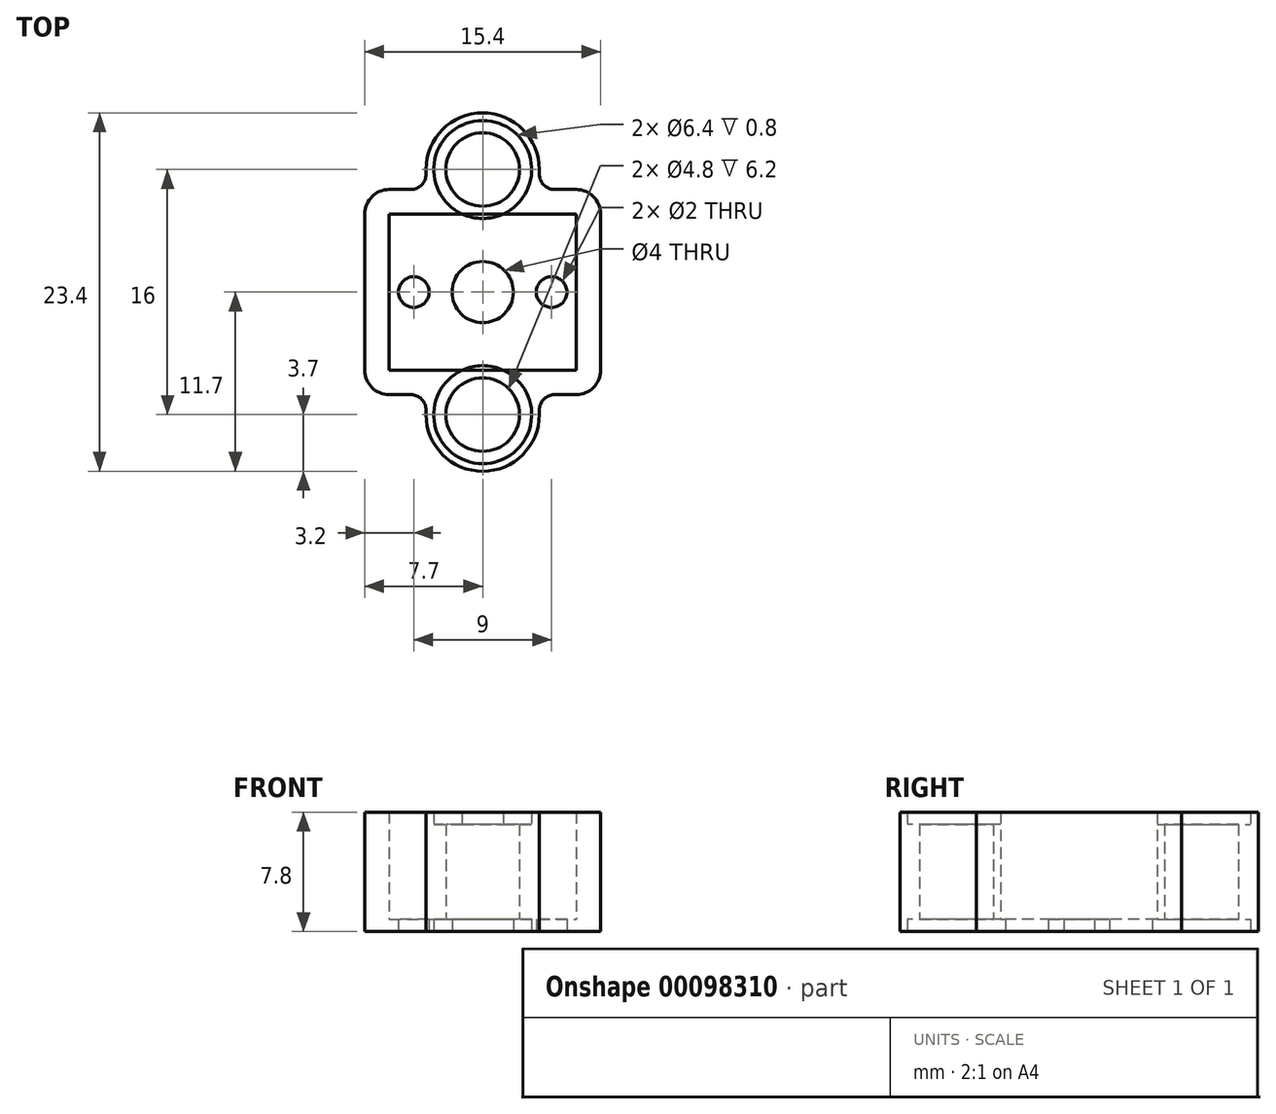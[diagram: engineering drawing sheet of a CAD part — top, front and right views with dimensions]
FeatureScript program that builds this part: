
annotation { "Feature Type Name" : "Feature", "Feature Type Description" : "" }
export const myFeature = defineFeature(function(context is Context, id is Id, definition is map)
    precondition{}
    {
        {
            var Q0;
            Q0=qCreatedBy(makeId("Top.planeOp"),FACE);
            var sketch = newSketch(context, id + "F0", { "sketchPlane" : qUnion([Q0])});
            skLineSegment(sketch, "E0.bottom", {"start": v(0, 11.7) * mm, "end": v(0, 11.7) * mm});
            skLineSegment(sketch, "E0.top", {"start": v(0, -11.7) * mm, "end": v(0, -11.7) * mm});
            skLineSegment(sketch, "E0.left", {"start": v(-3.7, 8) * mm, "end": v(-3.7, 7.7) * mm});
            skLineSegment(sketch, "E0.right", {"start": v(3.7, 8) * mm, "end": v(3.7, 7.7) * mm});
            skPoint(sketch, "E1.visualSharp", {"position": v(3.7, 11.7) * mm});
            skArc(sketch, "E1.filletArc", {"start": v(3.7, 8) * mm, "mid": v(2.62, 10.62) * mm, "end": v(0, 11.7) * mm});
            skPoint(sketch, "E2.visualSharp", {"position": v(3.7, -11.7) * mm});
            skArc(sketch, "E2.filletArc", {"start": v(0, -11.7) * mm, "mid": v(2.62, -10.62) * mm, "end": v(3.7, -8) * mm});
            skPoint(sketch, "E3.visualSharp", {"position": v(-3.7, -11.7) * mm});
            skArc(sketch, "E3.filletArc", {"start": v(-3.7, -8) * mm, "mid": v(-2.62, -10.62) * mm, "end": v(0, -11.7) * mm});
            skPoint(sketch, "E4.visualSharp", {"position": v(-3.7, 11.7) * mm});
            skArc(sketch, "E4.filletArc", {"start": v(0, 11.7) * mm, "mid": v(-2.62, 10.62) * mm, "end": v(-3.7, 8) * mm});
            skCircle(sketch, "E5", {"center": v(0, 8) * mm, "radius": 2.4 * mm});
            skCircle(sketch, "E6", {"center": v(0, -8) * mm, "radius": 2.4 * mm});
            skLineSegment(sketch, "E7.bottom", {"start": v(-6.1, 5.1) * mm, "end": v(6.1, 5.1) * mm});
            skLineSegment(sketch, "E7.top", {"start": v(-6.1, -5.1) * mm, "end": v(6.1, -5.1) * mm});
            skLineSegment(sketch, "E7.left", {"start": v(-6.1, 5.1) * mm, "end": v(-6.1, -5.1) * mm});
            skLineSegment(sketch, "E7.right", {"start": v(6.1, 5.1) * mm, "end": v(6.1, -5.1) * mm});
            skCircle(sketch, "E8", {"center": v(0, 0) * mm, "radius": 2 * mm});
            skCircle(sketch, "E9", {"center": v(4.5, 0) * mm, "radius": 1 * mm});
            skCircle(sketch, "E10", {"center": v(-4.5, 0) * mm, "radius": 1 * mm});
            skLineSegment(sketch, "E11.0", {"start": v(7.7, 5.1) * mm, "end": v(7.7, -5.1) * mm});
            skLineSegment(sketch, "E11.1", {"start": v(-6.1, 6.7) * mm, "end": v(-4.7, 6.7) * mm});
            skLineSegment(sketch, "E11.2", {"start": v(-7.7, 5.1) * mm, "end": v(-7.7, -5.1) * mm});
            skLineSegment(sketch, "E11.3", {"start": v(-6.1, -6.7) * mm, "end": v(-4.7, -6.7) * mm});
            skLineSegment(sketch, "E12.trimOffspring", {"start": v(4.7, 6.7) * mm, "end": v(6.1, 6.7) * mm});
            skLineSegment(sketch, "E13.trimOffspring", {"start": v(-3.7, -7.7) * mm, "end": v(-3.7, -8) * mm});
            skLineSegment(sketch, "E14.trimOffspring", {"start": v(4.7, -6.7) * mm, "end": v(6.1, -6.7) * mm});
            skLineSegment(sketch, "E15.trimOffspring", {"start": v(3.7, -7.7) * mm, "end": v(3.7, -8) * mm});
            skPoint(sketch, "E16.visualSharp", {"position": v(-7.7, 6.7) * mm});
            skArc(sketch, "E16.filletArc", {"start": v(-6.1, 6.7) * mm, "mid": v(-7.23, 6.23) * mm, "end": v(-7.7, 5.1) * mm});
            skPoint(sketch, "E17.visualSharp", {"position": v(7.7, 6.7) * mm});
            skArc(sketch, "E17.filletArc", {"start": v(7.7, 5.1) * mm, "mid": v(7.23, 6.23) * mm, "end": v(6.1, 6.7) * mm});
            skPoint(sketch, "E18.visualSharp", {"position": v(7.7, -6.7) * mm});
            skArc(sketch, "E18.filletArc", {"start": v(6.1, -6.7) * mm, "mid": v(7.23, -6.23) * mm, "end": v(7.7, -5.1) * mm});
            skPoint(sketch, "E19.visualSharp", {"position": v(-7.7, -6.7) * mm});
            skArc(sketch, "E19.filletArc", {"start": v(-7.7, -5.1) * mm, "mid": v(-7.23, -6.23) * mm, "end": v(-6.1, -6.7) * mm});
            skPoint(sketch, "E20.visualSharp", {"position": v(-3.7, -6.7) * mm});
            skArc(sketch, "E20.filletArc", {"start": v(-3.7, -7.7) * mm, "mid": v(-4, -7) * mm, "end": v(-4.7, -6.7) * mm});
            skPoint(sketch, "E21.visualSharp", {"position": v(3.7, -6.7) * mm});
            skArc(sketch, "E21.filletArc", {"start": v(4.7, -6.7) * mm, "mid": v(4, -7) * mm, "end": v(3.7, -7.7) * mm});
            skPoint(sketch, "E22.visualSharp", {"position": v(3.7, 6.7) * mm});
            skArc(sketch, "E22.filletArc", {"start": v(3.7, 7.7) * mm, "mid": v(4, 7) * mm, "end": v(4.7, 6.7) * mm});
            skPoint(sketch, "E23.visualSharp", {"position": v(-3.7, 6.7) * mm});
            skArc(sketch, "E23.filletArc", {"start": v(-4.7, 6.7) * mm, "mid": v(-4, 7) * mm, "end": v(-3.7, 7.7) * mm});
            skCircle(sketch, "E24", {"center": v(0, 8) * mm, "radius": 3.2 * mm});
            skCircle(sketch, "E25", {"center": v(0, -8) * mm, "radius": 3.2 * mm});
            skSolve(sketch);
        }
        {
            var Q0;
            Q0=makeQuery(id+"F0.imprint","IMPRINT",FACE,{"disambiguationData":[TD([[makeQuery(id+"F0.imprint","IMPRINT",EDGE,{"derivedFrom":sQuery(id+"F0.wireOp",EDGE,"E0.bottom")}),-1.0]])]});
            var Q1;
            Q1=makeQuery(id+"F0.imprint","IMPRINT",FACE,{"disambiguationData":[TD([[makeQuery(id+"F0.imprint","IMPRINT",EDGE,{"derivedFrom":sQuery(id+"F0.wireOp",EDGE,"E0.left")}),1.0]])]});
            extrude(context, id + "F1", {"entities" : qUnion([Q0, Q1]), "depth" : 7.8 * mm});
        }
        {
            var Q0;
            Q0=makeQuery(id+"F0.imprint","IMPRINT",FACE,{"disambiguationData":[TD([[makeQuery(id+"F0.imprint","IMPRINT",EDGE,{"derivedFrom":sQuery(id+"F0.wireOp",EDGE,"OhK9BFLk-ggx6-EKhq-4vyu-FNYu9IIR2aVE")}),-1.0]])]});
            var Q1;
            Q1=makeQuery(id+"F0.imprint","IMPRINT",FACE,{"disambiguationData":[TD([[makeQuery(id+"F0.imprint","IMPRINT",EDGE,{"derivedFrom":sQuery(id+"F0.wireOp",EDGE,"b0cbKfRL-Fema-Qfbk-Bb2r-JHD42yeqqMk3")}),1.0]])]});
            var Q2;
            Q2=makeQuery(id+"F0.imprint","IMPRINT",FACE,{"disambiguationData":[TD([[makeQuery(id+"F0.imprint","IMPRINT",EDGE,{"derivedFrom":sQuery(id+"F0.wireOp",EDGE,"E6")}),-1.0]])]});
            var Q3;
            Q3=makeQuery(id+"F0.imprint","IMPRINT",FACE,{"disambiguationData":[TD([[makeQuery(id+"F0.imprint","IMPRINT",EDGE,{"derivedFrom":sQuery(id+"F0.wireOp",EDGE,"E5")}),-1.0]])]});
            extrude(context, id + "F2", {"entities" : qUnion([Q0, Q1, Q2, Q3]), "operationType" : NewBodyOperationType.ADD, "depth" : 7 * mm, "hasSecondDirection" : true, "secondDirectionOppositeDirection" : false, "secondDirectionDepth" : 0.8 * mm});
        }
        {
            var Q0;
            {var subQ9=sQuery(id+"F0.wireOp",EDGE,"E7.left");Q0=makeQuery(id+"F0.imprint","IMPRINT",FACE,{"disambiguationData":[TD([[makeQuery(id+"F0.imprint","IMPRINT",EDGE,{"derivedFrom":subQ9}),1.0]])]});}
            extrude(context, id + "F3", {"entities" : qUnion([Q0]), "operationType" : NewBodyOperationType.ADD, "depth" : 0.8 * mm});
        }
    });
